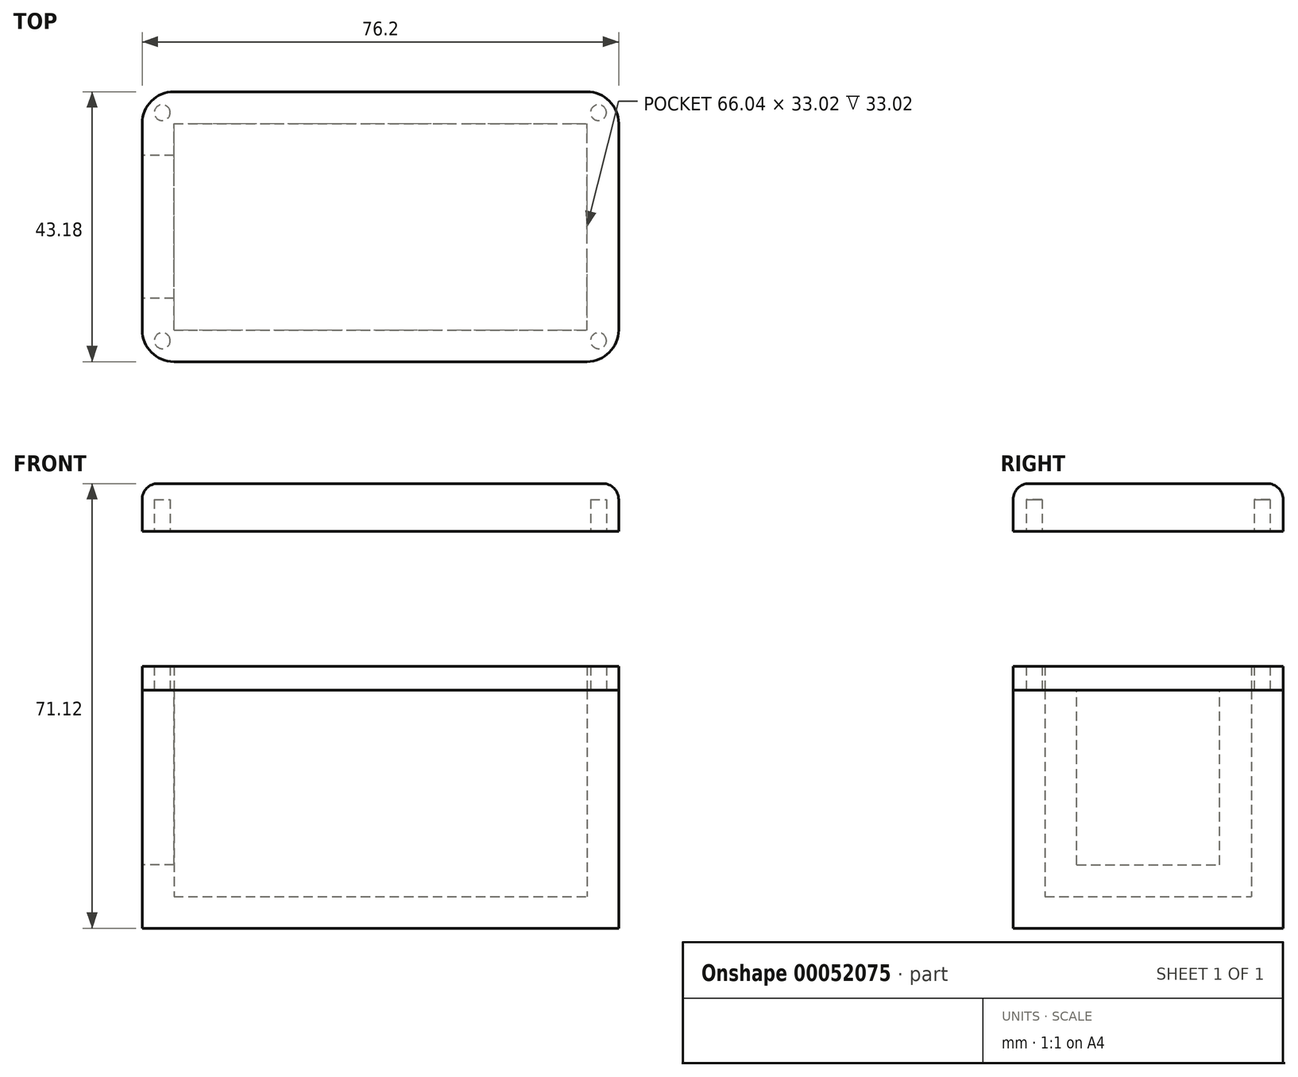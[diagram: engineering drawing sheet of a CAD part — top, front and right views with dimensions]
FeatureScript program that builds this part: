
annotation { "Feature Type Name" : "Feature", "Feature Type Description" : "" }
export const myFeature = defineFeature(function(context is Context, id is Id, definition is map)
    precondition{}
    {
        {
            var Q0;
            Q0=qCreatedBy(makeId("Top.planeOp"),FACE);
            var sketch = newSketch(context, id + "F0", { "sketchPlane" : qUnion([Q0])});
            skLineSegment(sketch, "E0.bottom", {"start": v(0, 0) * mm, "end": v(76.2, 0) * mm});
            skLineSegment(sketch, "E0.top", {"start": v(0, 43.18) * mm, "end": v(76.2, 43.18) * mm});
            skLineSegment(sketch, "E0.left", {"start": v(0, 0) * mm, "end": v(0, 43.18) * mm});
            skLineSegment(sketch, "E0.right", {"start": v(76.2, 0) * mm, "end": v(76.2, 43.18) * mm});
            skSolve(sketch);
        }
        {
            var Q0;
            Q0=makeQuery(id+"F0.imprint","IMPRINT",FACE,{"disambiguationData":[TD([[makeQuery(id+"F0.imprint","IMPRINT",EDGE,{"derivedFrom":sQuery(id+"F0.wireOp",EDGE,"E0.bottom")}),1.0]])]});
            extrude(context, id + "F1", {"entities" : qUnion([Q0]), "depth" : 38.1 * mm});
        }
        {
            var Q0;
            Q0=makeQuery(id+"F1.opExtrude","CAP_FACE",FACE,{"disambiguationData":[OSD([sQuery(id+"F0.wireOp",EDGE,"E0.bottom"),sQuery(id+"F0.wireOp",EDGE,"E0.top"),sQuery(id+"F0.wireOp",EDGE,"E0.left"),sQuery(id+"F0.wireOp",EDGE,"E0.right")])],"isStart":false});
            shell(context, id + "F2", {"entities" : qUnion([Q0]), "thickness" : 5.08 * mm});
        }
        {
            var Q0;
            Q0=makeQuery(id+"F1.opExtrude","SWEPT_EDGE",EDGE,{"disambiguationData":[OSD([sQuery(id+"F0.wireOp",EDGE,"E0.top"),sQuery(id+"F0.wireOp",EDGE,"E0.right")])]});
            var Q1;
            Q1=makeQuery(id+"F1.opExtrude","SWEPT_EDGE",EDGE,{"disambiguationData":[OSD([sQuery(id+"F0.wireOp",EDGE,"E0.bottom"),sQuery(id+"F0.wireOp",EDGE,"E0.right")])]});
            var Q2;
            Q2=makeQuery(id+"F1.opExtrude","SWEPT_EDGE",EDGE,{"disambiguationData":[OSD([sQuery(id+"F0.wireOp",EDGE,"E0.bottom"),sQuery(id+"F0.wireOp",EDGE,"E0.left")])]});
            var Q3;
            Q3=makeQuery(id+"F1.opExtrude","SWEPT_EDGE",EDGE,{"disambiguationData":[OSD([sQuery(id+"F0.wireOp",EDGE,"E0.top"),sQuery(id+"F0.wireOp",EDGE,"E0.left")])]});
            fillet(context, id + "F3", {"entities" : qUnion([Q0, Q1, Q2, Q3]), "radius" : 5.08 * mm, "tangentPropagation" : true, "allowEdgeOverflow" : false});
        }
        {
            var Q0;
            Q0=makeQuery(id+"F1.opExtrude","CAP_FACE",FACE,{"disambiguationData":[OSD([sQuery(id+"F0.wireOp",EDGE,"E0.bottom"),sQuery(id+"F0.wireOp",EDGE,"E0.top"),sQuery(id+"F0.wireOp",EDGE,"E0.left"),sQuery(id+"F0.wireOp",EDGE,"E0.right")])],"isStart":false});
            var sketch = newSketch(context, id + "F4", { "sketchPlane" : qUnion([Q0])});
            skCircle(sketch, "E1", {"center": v(3.22, 39.83) * mm, "radius": 1.27 * mm});
            skLineSegment(sketch, "E2", {"start": v(38.1, 43.18) * mm, "end": v(38.1, 0) * mm, "construction": true});
            skLineSegment(sketch, "E3", {"start": v(0, 21.6) * mm, "end": v(76.2, 21.6) * mm, "construction": true});
            skCircle(sketch, "E4.MirrorC", {"center": v(72.98, 39.83) * mm, "radius": 1.27 * mm});
            skCircle(sketch, "E5.MirrorC", {"center": v(72.98, 3.35) * mm, "radius": 1.27 * mm});
            skCircle(sketch, "E6.MirrorC", {"center": v(3.22, 3.35) * mm, "radius": 1.27 * mm});
            skSolve(sketch);
        }
        {
            var Q0;
            Q0=makeQuery(id+"F4.imprint","IMPRINT",FACE,{"disambiguationData":[TD([[makeQuery(id+"F4.imprint","IMPRINT",EDGE,{"derivedFrom":sQuery(id+"F4.wireOp",EDGE,"E6.MirrorC")}),-1.0]])]});
            var Q1;
            Q1=makeQuery(id+"F4.imprint","IMPRINT",FACE,{"disambiguationData":[TD([[makeQuery(id+"F4.imprint","IMPRINT",EDGE,{"derivedFrom":sQuery(id+"F4.wireOp",EDGE,"E1")}),1.0]])]});
            var Q2;
            Q2=makeQuery(id+"F4.imprint","IMPRINT",FACE,{"disambiguationData":[TD([[makeQuery(id+"F4.imprint","IMPRINT",EDGE,{"derivedFrom":sQuery(id+"F4.wireOp",EDGE,"E5.MirrorC")}),1.0]])]});
            var Q3;
            Q3=makeQuery(id+"F4.imprint","IMPRINT",FACE,{"disambiguationData":[TD([[makeQuery(id+"F4.imprint","IMPRINT",EDGE,{"derivedFrom":sQuery(id+"F4.wireOp",EDGE,"E4.MirrorC")}),-1.0]])]});
            var Q4;
            Q4=sQuery(id+"F4.wireOp",EDGE,"E6.MirrorC");
            var Q5;
            Q5=sQuery(id+"F4.wireOp",EDGE,"E5.MirrorC");
            var Q6;
            Q6=sQuery(id+"F4.wireOp",EDGE,"E4.MirrorC");
            var Q7;
            Q7=sQuery(id+"F4.wireOp",EDGE,"E1");
            extrude(context, id + "F5", {"entities" : qUnion([Q0, Q1, Q2, Q3]), "surfaceEntities" : qUnion([Q4, Q5, Q6, Q7]), "depth" : 3.8 * mm});
        }
        {
            var Q0;
            Q0=makeQuery(id+"F1.opExtrude","CAP_FACE",FACE,{"disambiguationData":[OSD([sQuery(id+"F0.wireOp",EDGE,"E0.bottom"),sQuery(id+"F0.wireOp",EDGE,"E0.top"),sQuery(id+"F0.wireOp",EDGE,"E0.left"),sQuery(id+"F0.wireOp",EDGE,"E0.right")])],"isStart":false});
            cPlane(context, id + "F6", {"entities" : qUnion([Q0]), "cplaneType" : CPlaneType.OFFSET, "offset" : 25.4 * mm, "width" : 152.4 * mm, "height" : 152.4 * mm});
        }
        {
            var Q0;
            Q0=qCreatedBy(id+"F6.planeOp",FACE);
            var sketch = newSketch(context, id + "F7", { "sketchPlane" : qUnion([Q0])});
            skLineSegment(sketch, "E7.0.0", {"start": v(5.08, 38.1) * mm, "end": v(5.08, 5.08) * mm});
            skLineSegment(sketch, "E7.0.1", {"start": v(5.08, 5.08) * mm, "end": v(71.12, 5.08) * mm});
            skLineSegment(sketch, "E7.0.2", {"start": v(71.12, 5.08) * mm, "end": v(71.12, 38.1) * mm});
            skLineSegment(sketch, "E7.0.3", {"start": v(71.12, 38.1) * mm, "end": v(5.08, 38.1) * mm});
            skLineSegment(sketch, "E8.0", {"start": v(71.12, 43.18) * mm, "end": v(5.08, 43.18) * mm});
            skLineSegment(sketch, "E8.1", {"start": v(76.2, 5.08) * mm, "end": v(76.2, 38.1) * mm});
            skLineSegment(sketch, "E8.2", {"start": v(5.08, 0) * mm, "end": v(71.12, 0) * mm});
            skLineSegment(sketch, "E8.3", {"start": v(0, 38.1) * mm, "end": v(0, 5.08) * mm});
            skPoint(sketch, "E9.visualSharp", {"position": v(0, 43.18) * mm});
            skArc(sketch, "E9.filletArc", {"start": v(5.08, 43.18) * mm, "mid": v(1.49, 41.7) * mm, "end": v(0, 38.1) * mm});
            skPoint(sketch, "E10.visualSharp", {"position": v(0, 0) * mm});
            skArc(sketch, "E10.filletArc", {"start": v(0, 5.08) * mm, "mid": v(1.49, 1.49) * mm, "end": v(5.08, 0) * mm});
            skPoint(sketch, "E11.visualSharp", {"position": v(76.2, 0) * mm});
            skArc(sketch, "E11.filletArc", {"start": v(71.12, 0) * mm, "mid": v(74.71, 1.49) * mm, "end": v(76.2, 5.08) * mm});
            skPoint(sketch, "E12.visualSharp", {"position": v(76.2, 43.18) * mm});
            skArc(sketch, "E12.filletArc", {"start": v(76.2, 38.1) * mm, "mid": v(74.71, 41.7) * mm, "end": v(71.12, 43.18) * mm});
            skSolve(sketch);
        }
        {
            var Q0;
            Q0=makeQuery(id+"F7.imprint","IMPRINT",FACE,{"disambiguationData":[TD([[makeQuery(id+"F7.imprint","IMPRINT",EDGE,{"derivedFrom":sQuery(id+"F7.wireOp",EDGE,"E7.0.0")}),-1.0]])]});
            var Q1;
            Q1=makeQuery(id+"F7.imprint","IMPRINT",FACE,{"disambiguationData":[TD([[makeQuery(id+"F7.imprint","IMPRINT",EDGE,{"derivedFrom":sQuery(id+"F7.wireOp",EDGE,"E7.0.0")}),1.0]])]});
            extrude(context, id + "F8", {"entities" : qUnion([Q0, Q1]), "depth" : 7.62 * mm});
        }
        {
            var Q0;
            Q0=makeQuery(id+"F8.opExtrude","CAP_FACE",FACE,{"disambiguationData":[OSD([sQuery(id+"F7.wireOp",EDGE,"E8.0"),sQuery(id+"F7.wireOp",EDGE,"E8.1"),sQuery(id+"F7.wireOp",EDGE,"E8.2"),sQuery(id+"F7.wireOp",EDGE,"E8.3"),sQuery(id+"F7.wireOp",EDGE,"E9.filletArc"),sQuery(id+"F7.wireOp",EDGE,"E10.filletArc"),sQuery(id+"F7.wireOp",EDGE,"E11.filletArc"),sQuery(id+"F7.wireOp",EDGE,"E12.filletArc")])],"isStart":true});
            var sketch = newSketch(context, id + "F9", { "sketchPlane" : qUnion([Q0])});
            skCircle(sketch, "E13.0", {"center": v(3.22, -3.35) * mm, "radius": 1.27 * mm});
            skCircle(sketch, "E14.0", {"center": v(72.98, -3.35) * mm, "radius": 1.27 * mm});
            skCircle(sketch, "E15.0", {"center": v(72.98, -39.83) * mm, "radius": 1.27 * mm});
            skCircle(sketch, "E16.0", {"center": v(3.22, -39.83) * mm, "radius": 1.27 * mm});
            skSolve(sketch);
        }
        {
            var Q0;
            Q0 = qSketchRegion(id + "F9", true);
            extrude(context, id + "F10", {"entities" : qUnion([Q0]), "operationType" : NewBodyOperationType.REMOVE, "oppositeDirection" : true, "depth" : 5.08 * mm});
        }
        {
            var Q0;
            Q0=makeQuery(id+"F8.opExtrude","CAP_FACE",FACE,{"disambiguationData":[OSD([sQuery(id+"F7.wireOp",EDGE,"E8.0"),sQuery(id+"F7.wireOp",EDGE,"E8.1"),sQuery(id+"F7.wireOp",EDGE,"E8.2"),sQuery(id+"F7.wireOp",EDGE,"E8.3"),sQuery(id+"F7.wireOp",EDGE,"E9.filletArc"),sQuery(id+"F7.wireOp",EDGE,"E10.filletArc"),sQuery(id+"F7.wireOp",EDGE,"E11.filletArc"),sQuery(id+"F7.wireOp",EDGE,"E12.filletArc")])],"isStart":false});
            fillet(context, id + "F11", {"entities" : qUnion([Q0]), "radius" : 2.54 * mm, "tangentPropagation" : true, "allowEdgeOverflow" : false});
        }
        {
            var Q0;
            Q0=makeQuery(id+"F1.opExtrude","SWEPT_FACE",FACE,{"disambiguationData":[OSD([sQuery(id+"F0.wireOp",EDGE,"E0.left")])]});
            var sketch = newSketch(context, id + "F12", { "sketchPlane" : qUnion([Q0])});
            skLineSegment(sketch, "E17.bottom", {"start": v(-33.02, 38.1) * mm, "end": v(-10.16, 38.1) * mm});
            skLineSegment(sketch, "E17.top", {"start": v(-33.02, 10.16) * mm, "end": v(-10.16, 10.16) * mm});
            skLineSegment(sketch, "E17.left", {"start": v(-33.02, 38.1) * mm, "end": v(-33.02, 10.16) * mm});
            skLineSegment(sketch, "E17.right", {"start": v(-10.16, 38.1) * mm, "end": v(-10.16, 10.16) * mm});
            skSolve(sketch);
        }
        {
            var Q0;
            Q0=makeQuery(id+"F12.imprint","IMPRINT",FACE,{"disambiguationData":[TD([[makeQuery(id+"F12.imprint","IMPRINT",EDGE,{"derivedFrom":sQuery(id+"F12.wireOp",EDGE,"E17.bottom")}),1.0]])]});
            extrude(context, id + "F13", {"entities" : qUnion([Q0]), "operationType" : NewBodyOperationType.REMOVE, "endBound" : BoundingType.UP_TO_NEXT, "oppositeDirection" : true, "depth" : 25.4 * mm});
        }
    });
